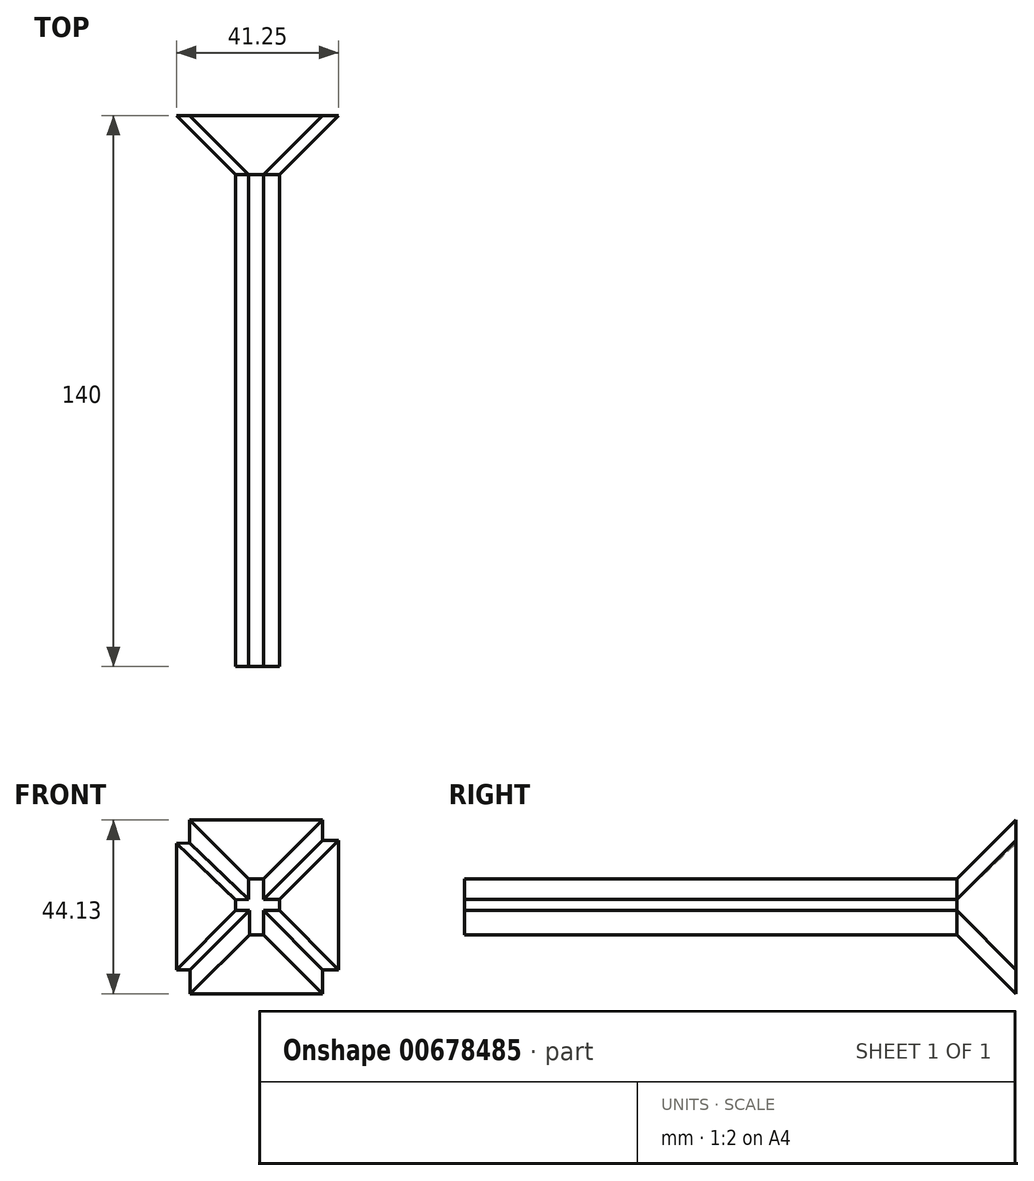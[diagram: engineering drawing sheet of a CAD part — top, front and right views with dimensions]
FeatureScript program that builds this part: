
annotation { "Feature Type Name" : "Feature", "Feature Type Description" : "" }
export const myFeature = defineFeature(function(context is Context, id is Id, definition is map)
    precondition{}
    {
        {
            var Q0;
            Q0=qCreatedBy(makeId("Front.planeOp"),FACE);
            var sketch = newSketch(context, id + "F0", { "sketchPlane" : qUnion([Q0])});
            skLineSegment(sketch, "E0", {"start": v(-2.09, 6.78) * mm, "end": v(1.77, 6.78) * mm});
            skLineSegment(sketch, "E1", {"start": v(1.77, 6.78) * mm, "end": v(1.77, 1.55) * mm});
            skLineSegment(sketch, "E2", {"start": v(-2.09, 6.78) * mm, "end": v(-2.09, 1.55) * mm});
            skLineSegment(sketch, "E3", {"start": v(1.77, 1.55) * mm, "end": v(5.84, 1.55) * mm});
            skLineSegment(sketch, "E4", {"start": v(5.84, 1.55) * mm, "end": v(5.84, -1.25) * mm});
            skLineSegment(sketch, "E5", {"start": v(5.84, -1.25) * mm, "end": v(1.77, -1.25) * mm});
            skLineSegment(sketch, "E6", {"start": v(1.77, -1.25) * mm, "end": v(1.77, -7.35) * mm});
            skLineSegment(sketch, "E7", {"start": v(1.77, -7.35) * mm, "end": v(-1.87, -7.35) * mm});
            skLineSegment(sketch, "E8", {"start": v(-1.87, -7.35) * mm, "end": v(-1.87, -1.25) * mm});
            skLineSegment(sketch, "E9", {"start": v(-1.87, -1.25) * mm, "end": v(-5.4, -1.25) * mm});
            skLineSegment(sketch, "E10", {"start": v(-5.4, -1.25) * mm, "end": v(-5.4, 1.55) * mm});
            skLineSegment(sketch, "E11", {"start": v(-5.4, 1.43) * mm, "end": v(-2.09, 1.55) * mm});
            skSolve(sketch);
        }
        {
            var Q0;
            Q0=makeQuery(id+"F0.imprint","IMPRINT",FACE,{"disambiguationData":[TD([[makeQuery(id+"F0.imprint","IMPRINT",EDGE,{"derivedFrom":sQuery(id+"F0.wireOp",EDGE,"E0")}),-1.0]])]});
            extrude(context, id + "F1", {"entities" : qUnion([Q0]), "depth" : 125 * mm, "offsetDistance" : 25 * mm});
        }
        {
            var Q0;
            Q0=makeQuery(id+"F1.opExtrude","CAP_FACE",FACE,{"disambiguationData":[OSD([sQuery(id+"F0.wireOp",EDGE,"E0"),sQuery(id+"F0.wireOp",EDGE,"E1"),sQuery(id+"F0.wireOp",EDGE,"E2"),sQuery(id+"F0.wireOp",EDGE,"E3"),sQuery(id+"F0.wireOp",EDGE,"E4"),sQuery(id+"F0.wireOp",EDGE,"E5"),sQuery(id+"F0.wireOp",EDGE,"E6"),sQuery(id+"F0.wireOp",EDGE,"E7"),sQuery(id+"F0.wireOp",EDGE,"E8"),sQuery(id+"F0.wireOp",EDGE,"E9"),sQuery(id+"F0.wireOp",EDGE,"E10"),sQuery(id+"F0.wireOp",EDGE,"E11")])],"isStart":true});
            extrude(context, id + "F2", {"entities" : qUnion([Q0]), "operationType" : NewBodyOperationType.ADD, "depth" : 15 * mm, "offsetDistance" : 25 * mm, "hasDraft" : true, "draftAngle" : 45 * degree});
        }
    });
